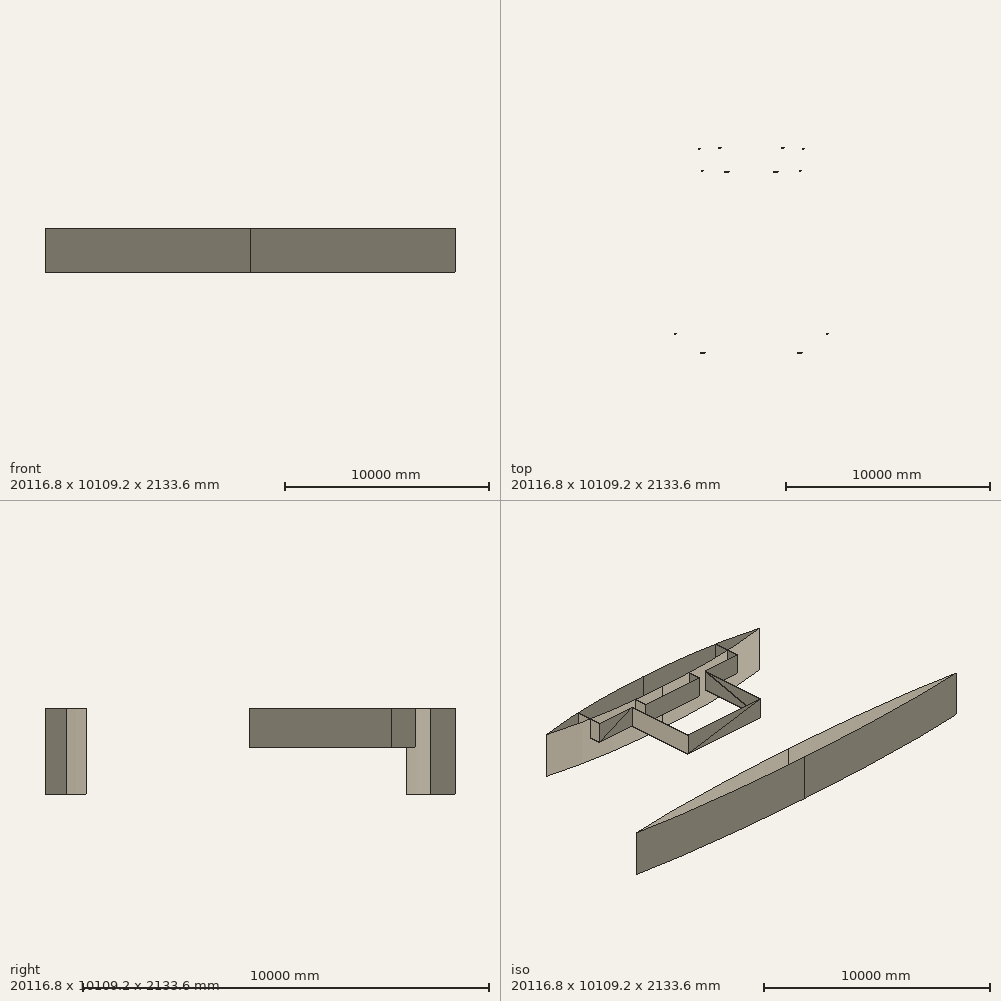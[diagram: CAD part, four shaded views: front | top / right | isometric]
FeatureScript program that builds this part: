
annotation { "Feature Type Name" : "Feature", "Feature Type Description" : "" }
export const myFeature = defineFeature(function(context is Context, id is Id, definition is map)
    precondition{}
    {
        {
            var Q0;
            Q0=qCreatedBy(makeId("Top.planeOp"),FACE);
            var sketch = newSketch(context, id + "F0", { "sketchPlane" : qUnion([Q0])});
            skPoint(sketch, "E0.middle", {"position": v(0, 0) * mm});
            skLineSegment(sketch, "E1", {"start": v(0, 5105.4) * mm, "end": v(0, 3886.2) * mm});
            skFitSpline(sketch, "E2", {"points": [v(-10058.4, -4495.8) * mm, v(0, -3987.8) * mm], "startDerivative": vector(11545.6, 1524) * mm, "endDerivative": vector(2997.78, 0) * mm});
            skFitSpline(sketch, "E3.MirrorCS", {"points": [v(-10058.4, -4495.8) * mm, v(0, -5003.8) * mm], "startDerivative": vector(11545.6, -1524) * mm, "endDerivative": vector(2997.78, 0) * mm});
            skFitSpline(sketch, "E4.MirrorCS", {"points": [v(10058.4, -4495.8) * mm, v(0, -3987.8) * mm], "startDerivative": vector(-11545.6, 1524) * mm, "endDerivative": vector(-2997.78, 0) * mm});
            skFitSpline(sketch, "E5.MirrorCS", {"points": [v(10058.4, -4495.8) * mm, v(0, -5003.8) * mm], "startDerivative": vector(-11545.6, -1524) * mm, "endDerivative": vector(-2997.78, 0) * mm});
            skFitSpline(sketch, "E6", {"points": [v(-6705.6, 4495.8) * mm, v(0, 5105.4) * mm], "startDerivative": vector(8549.77, 1828.8) * mm, "endDerivative": vector(3280.28, 0) * mm});
            skFitSpline(sketch, "E7.MirrorCS", {"points": [v(6705.6, 4495.8) * mm, v(0, 5105.4) * mm], "startDerivative": vector(-8549.77, 1828.8) * mm, "endDerivative": vector(-3280.28, 0) * mm});
            skFitSpline(sketch, "E8.MirrorCS", {"points": [v(-6705.6, 4495.8) * mm, v(0, 3886.2) * mm], "startDerivative": vector(8549.77, -1828.8) * mm, "endDerivative": vector(3280.28, 0) * mm});
            skFitSpline(sketch, "E9.MirrorCS", {"points": [v(6705.6, 4495.8) * mm, v(0, 3886.2) * mm], "startDerivative": vector(-8549.77, -1828.8) * mm, "endDerivative": vector(-3280.28, 0) * mm});
            skLineSegment(sketch, "E10", {"start": v(-4318, 3529.05) * mm, "end": v(-2286, 3529.05) * mm});
            skLineSegment(sketch, "E11", {"start": v(-2286, 3529.05) * mm, "end": v(-2286, 5053.05) * mm});
            skLineSegment(sketch, "E12.MirrorCS", {"start": v(2286, 3529.05) * mm, "end": v(2286, 5053.05) * mm});
            skLineSegment(sketch, "E13.MirrorCS", {"start": v(4318, 3529.05) * mm, "end": v(2286, 3529.05) * mm});
            skLineSegment(sketch, "E14", {"start": v(-1676.4, 5079.88) * mm, "end": v(-1676.4, 3911.72) * mm});
            skLineSegment(sketch, "E15", {"start": v(-2286, 3529.05) * mm, "end": v(-2286, 25.4) * mm});
            skLineSegment(sketch, "E16", {"start": v(-1676.4, 3911.72) * mm, "end": v(-1676.4, 3276.6) * mm});
            skLineSegment(sketch, "E17", {"start": v(-1676.4, 3276.6) * mm, "end": v(0, 3276.6) * mm});
            skLineSegment(sketch, "E18", {"start": v(-2286, 25.4) * mm, "end": v(0, 25.4) * mm});
            skLineSegment(sketch, "E19.MirrorCS", {"start": v(2286, 3529.05) * mm, "end": v(2286, 25.4) * mm});
            skLineSegment(sketch, "E20.MirrorCS", {"start": v(2286, 25.4) * mm, "end": v(0, 25.4) * mm});
            skLineSegment(sketch, "E21.MirrorCS", {"start": v(1676.4, 3276.6) * mm, "end": v(0, 3276.6) * mm});
            skLineSegment(sketch, "E22.MirrorCS", {"start": v(1676.4, 3911.72) * mm, "end": v(1676.4, 3276.6) * mm});
            skLineSegment(sketch, "E23", {"start": v(1676.4, 3911.72) * mm, "end": v(1676.4, 5079.88) * mm});
            skLineSegment(sketch, "E24", {"start": v(4318, 3529.05) * mm, "end": v(4318, 4883.61) * mm});
            skLineSegment(sketch, "E25", {"start": v(-4318, 3529.05) * mm, "end": v(-4318, 4883.61) * mm});
            skSolve(sketch);
        }
        {
            var Q0;
            Q0=sQuery(id+"F0.wireOp",EDGE,"E6");
            var Q1;
            Q1=sQuery(id+"F0.wireOp",EDGE,"E8.MirrorCS");
            var Q2;
            Q2=sQuery(id+"F0.wireOp",EDGE,"E9.MirrorCS");
            var Q3;
            Q3=sQuery(id+"F0.wireOp",EDGE,"E7.MirrorCS");
            var Q4;
            Q4=sQuery(id+"F0.wireOp",EDGE,"E4.MirrorCS");
            var Q5;
            Q5=sQuery(id+"F0.wireOp",EDGE,"E5.MirrorCS");
            var Q6;
            Q6=sQuery(id+"F0.wireOp",EDGE,"E2");
            var Q7;
            Q7=sQuery(id+"F0.wireOp",EDGE,"E3.MirrorCS");
            extrude(context, id + "F1", {"bodyType" : ToolBodyType.SURFACE, "surfaceEntities" : qUnion([Q0, Q1, Q2, Q3, Q4, Q5, Q6, Q7]), "oppositeDirection" : true, "depth" : 2133.6 * mm});
        }
        {
            var Q0;
            Q0 = qSketchRegion(id + "F0", true);
            var Q1;
            Q1=sQuery(id+"F0.wireOp",EDGE,"E10");
            var Q2;
            Q2=sQuery(id+"F0.wireOp",EDGE,"E18");
            var Q3;
            Q3=sQuery(id+"F0.wireOp",EDGE,"E20.MirrorCS");
            var Q4;
            Q4=sQuery(id+"F0.wireOp",EDGE,"E19.MirrorCS");
            var Q5;
            Q5=sQuery(id+"F0.wireOp",EDGE,"E13.MirrorCS");
            var Q6;
            Q6=sQuery(id+"F0.wireOp",EDGE,"E15");
            var Q7;
            Q7=sQuery(id+"F0.wireOp",EDGE,"E24");
            var Q8;
            Q8=sQuery(id+"F0.wireOp",EDGE,"E25");
            extrude(context, id + "F2", {"entities" : qUnion([Q0]), "bodyType" : ToolBodyType.SURFACE, "surfaceEntities" : qUnion([Q1, Q2, Q3, Q4, Q5, Q6, Q7, Q8]), "depth" : -965.2 * mm});
        }
        {
            var Q0;
            Q0 = qSketchRegion(id + "F0", true);
            var Q1;
            Q1=sQuery(id+"F0.wireOp",EDGE,"E15");
            var Q2;
            Q2=sQuery(id+"F0.wireOp",EDGE,"E10");
            var Q3;
            Q3=sQuery(id+"F0.wireOp",EDGE,"E16");
            var Q4;
            Q4=sQuery(id+"F0.wireOp",EDGE,"E17");
            var Q5;
            Q5=sQuery(id+"F0.wireOp",EDGE,"E21.MirrorCS");
            var Q6;
            Q6=sQuery(id+"F0.wireOp",EDGE,"E22.MirrorCS");
            var Q7;
            Q7=sQuery(id+"F0.wireOp",EDGE,"E13.MirrorCS");
            var Q8;
            Q8=sQuery(id+"F0.wireOp",EDGE,"E19.MirrorCS");
            var Q9;
            Q9=sQuery(id+"F0.wireOp",EDGE,"E20.MirrorCS");
            var Q10;
            Q10=sQuery(id+"F0.wireOp",EDGE,"E18");
            var Q11;
            Q11=sQuery(id+"F0.wireOp",EDGE,"syRZxJZq-BmSD-5gDi-SCNs-ntcT0XnGbHXO");
            extrude(context, id + "F3", {"entities" : qUnion([Q0]), "bodyType" : ToolBodyType.SURFACE, "surfaceEntities" : qUnion([Q1, Q2, Q3, Q4, Q5, Q6, Q7, Q8, Q9, Q10, Q11]), "oppositeDirection" : true, "depth" : 965.2 * mm});
        }
    });
